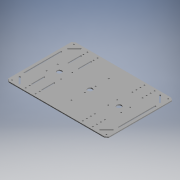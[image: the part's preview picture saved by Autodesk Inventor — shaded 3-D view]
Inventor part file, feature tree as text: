
AUTODESK INVENTOR PART (.ipt)
format: ipt  version: 2019 (Build 230136000, 136)  size: 278,528 bytes
history: native  units: mm (DEFAULTED — no unit token found)
features: extrude x1, sketch x1
ambient origin geometry x8: Origin, YZ Plane, XZ Plane, XY Plane, X Axis, Y Axis, Z Axis, Center Point
bodies: Body1 (feature_tree)
feature tree (2):
  extrude  "Extrusion2"  Depth=200.0mm
  sketch  "Sketch1"  dims[d0=300.0mm d1=200.0mm d2=8.0mm d3=5.5mm d4=5.5mm d5=8.0mm d6=8.0mm d7=5.5mm d8=5.5mm d9=8.0mm d10=8.0mm d11=4.0mm d12=4.0mm d13=4.0mm d14=9.5mm d15=50.0mm d16=80.0mm d17=4.0mm d18=4.0mm d19=4.0mm d20=9.5mm d21=50.0mm d22=80.0mm d23=4.0mm d24=4.0mm d25=4.0mm d26=44.0mm d27=32.0mm d28=20.0mm d29=4.0mm d30=4.0mm d31=4.0mm d32=20.0mm d33=32.0mm d34=44.0mm d35=4.0mm d36=4.0mm d37=20.0mm d38=20.0mm d39=4.0mm d40=4.0mm d41=7.5mm d42=7.5mm d43=4.0mm d44=36.0mm d45=4.0mm d46=36.0mm d47=4.0mm d48=16.6mm d49=14.0mm d50=14.0mm d51=58.5mm d52=63.5mm d53=14.0mm d54=4.0mm d55=16.0mm d56=4.0mm d57=13.5mm d58=44.2mm d59=4.0mm d60=4.0mm d61=9.5mm d62=108.0mm d63=4.0mm d64=4.0mm d65=26.5mm d66=45.0deg d67=12.2mm d68=4.0mm d69=4.0mm d70=26.5mm d71=45.0deg d72=12.2mm d75=4.0mm d77=44.5mm d78=3.0mm d79=0.0mm]
